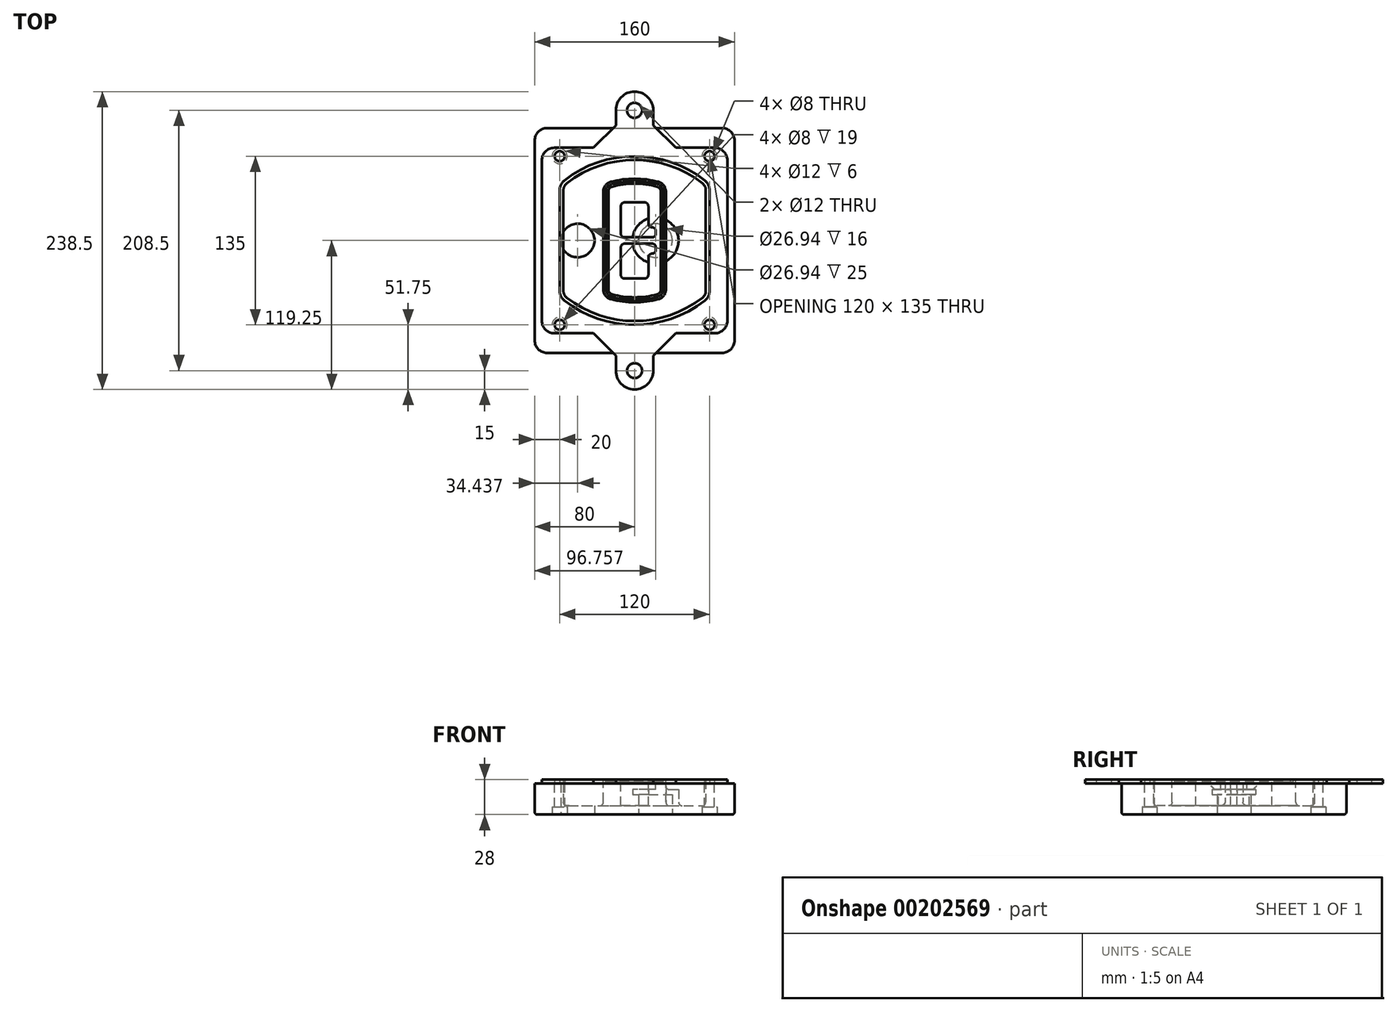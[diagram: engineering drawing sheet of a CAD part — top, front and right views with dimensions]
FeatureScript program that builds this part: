
annotation { "Feature Type Name" : "Feature", "Feature Type Description" : "" }
export const myFeature = defineFeature(function(context is Context, id is Id, definition is map)
    precondition{}
    {
        {
            var Q0;
            Q0=qCreatedBy(makeId("Top.planeOp"),FACE);
            var sketch = newSketch(context, id + "F0", { "sketchPlane" : qUnion([Q0])});
            skPoint(sketch, "E0.rect.middle", {"position": v(0, 0) * mm});
            skLineSegment(sketch, "E1.bottom", {"start": v(-70, -90) * mm, "end": v(70, -90) * mm});
            skLineSegment(sketch, "E1.top", {"start": v(-70, 90) * mm, "end": v(70, 90) * mm});
            skLineSegment(sketch, "E1.left", {"start": v(-80, -80) * mm, "end": v(-80, 80) * mm});
            skLineSegment(sketch, "E1.right", {"start": v(80, -80) * mm, "end": v(80, 80) * mm});
            skLineSegment(sketch, "E2", {"start": v(-80, 90) * mm, "end": v(80, -90) * mm, "construction": true});
            skLineSegment(sketch, "E3", {"start": v(80, 90) * mm, "end": v(-80, -90) * mm, "construction": true});
            skCircle(sketch, "E4", {"center": v(-60, 67.5) * mm, "radius": 4 * mm});
            skCircle(sketch, "E5", {"center": v(60, 67.5) * mm, "radius": 4 * mm});
            skCircle(sketch, "E6", {"center": v(60, -67.5) * mm, "radius": 4 * mm});
            skCircle(sketch, "E7", {"center": v(-60, -67.5) * mm, "radius": 4 * mm});
            skLineSegment(sketch, "E8", {"start": v(-60, 67.5) * mm, "end": v(60, 67.5) * mm, "construction": true});
            skLineSegment(sketch, "E9", {"start": v(60, 67.5) * mm, "end": v(60, -67.5) * mm, "construction": true});
            skLineSegment(sketch, "E10", {"start": v(60, -67.5) * mm, "end": v(-60, -67.5) * mm, "construction": true});
            skLineSegment(sketch, "E11", {"start": v(-60, -67.5) * mm, "end": v(-60, 67.5) * mm, "construction": true});
            skLineSegment(sketch, "E12", {"start": v(-60, 40.3) * mm, "end": v(-60, -40.3) * mm});
            skLineSegment(sketch, "E13", {"start": v(60, 40.3) * mm, "end": v(60, -40.3) * mm});
            skArc(sketch, "E14", {"start": v(56.15, 48.18) * mm, "mid": v(0, 67.5) * mm, "end": v(-56.15, 48.18) * mm});
            skArc(sketch, "E15", {"start": v(-56.15, -48.18) * mm, "mid": v(0, -67.5) * mm, "end": v(56.15, -48.18) * mm});
            skLineSegment(sketch, "E16", {"start": v(-60, 0) * mm, "end": v(60, 0) * mm, "construction": true});
            skPoint(sketch, "E17.visualSharp", {"position": v(-60, -45) * mm});
            skArc(sketch, "E17.filletArc", {"start": v(-60, -40.3) * mm, "mid": v(-58.99, -44.68) * mm, "end": v(-56.15, -48.18) * mm});
            skPoint(sketch, "E18.visualSharp", {"position": v(-60, 45) * mm});
            skArc(sketch, "E18.filletArc", {"start": v(-56.15, 48.18) * mm, "mid": v(-58.99, 44.68) * mm, "end": v(-60, 40.3) * mm});
            skPoint(sketch, "E19.visualSharp", {"position": v(60, 45) * mm});
            skArc(sketch, "E19.filletArc", {"start": v(60, 40.3) * mm, "mid": v(58.99, 44.68) * mm, "end": v(56.15, 48.18) * mm});
            skPoint(sketch, "E20.visualSharp", {"position": v(60, -45) * mm});
            skArc(sketch, "E20.filletArc", {"start": v(56.15, -48.18) * mm, "mid": v(58.99, -44.68) * mm, "end": v(60, -40.3) * mm});
            skPoint(sketch, "E21.visualSharp", {"position": v(-80, 90) * mm});
            skArc(sketch, "E21.filletArc", {"start": v(-70, 90) * mm, "mid": v(-77.07, 87.07) * mm, "end": v(-80, 80) * mm});
            skPoint(sketch, "E22.visualSharp", {"position": v(80, 90) * mm});
            skArc(sketch, "E22.filletArc", {"start": v(80, 80) * mm, "mid": v(77.07, 87.07) * mm, "end": v(70, 90) * mm});
            skPoint(sketch, "E23.visualSharp", {"position": v(80, -90) * mm});
            skArc(sketch, "E23.filletArc", {"start": v(70, -90) * mm, "mid": v(77.07, -87.07) * mm, "end": v(80, -80) * mm});
            skPoint(sketch, "E24.visualSharp", {"position": v(-80, -90) * mm});
            skArc(sketch, "E24.filletArc", {"start": v(-80, -80) * mm, "mid": v(-77.07, -87.07) * mm, "end": v(-70, -90) * mm});
            skArc(sketch, "E25.0", {"start": v(57, 40.3) * mm, "mid": v(56.3, 43.36) * mm, "end": v(54.3, 45.81) * mm});
            skLineSegment(sketch, "E25.1", {"start": v(57, 40.3) * mm, "end": v(57, -40.3) * mm});
            skArc(sketch, "E25.2", {"start": v(54.3, -45.81) * mm, "mid": v(56.3, -43.36) * mm, "end": v(57, -40.3) * mm});
            skArc(sketch, "E25.3", {"start": v(-54.3, -45.81) * mm, "mid": v(0, -64.5) * mm, "end": v(54.3, -45.81) * mm});
            skArc(sketch, "E25.4", {"start": v(-57, -40.3) * mm, "mid": v(-56.3, -43.36) * mm, "end": v(-54.3, -45.81) * mm});
            skArc(sketch, "E25.5", {"start": v(54.3, 45.81) * mm, "mid": v(0, 64.5) * mm, "end": v(-54.3, 45.81) * mm});
            skLineSegment(sketch, "E25.6", {"start": v(-57, 40.3) * mm, "end": v(-57, -40.3) * mm});
            skArc(sketch, "E25.7", {"start": v(-54.3, 45.81) * mm, "mid": v(-56.3, 43.36) * mm, "end": v(-57, 40.3) * mm});
            skArc(sketch, "E26.0", {"start": v(-58.62, 51.33) * mm, "mid": v(-62.58, 46.43) * mm, "end": v(-64, 40.3) * mm});
            skArc(sketch, "E26.1", {"start": v(58.62, 51.33) * mm, "mid": v(0, 71.5) * mm, "end": v(-58.62, 51.33) * mm});
            skArc(sketch, "E26.2", {"start": v(64, 40.3) * mm, "mid": v(62.58, 46.43) * mm, "end": v(58.62, 51.33) * mm});
            skLineSegment(sketch, "E26.3", {"start": v(64, 40.3) * mm, "end": v(64, -40.3) * mm});
            skArc(sketch, "E26.4", {"start": v(58.62, -51.33) * mm, "mid": v(62.58, -46.43) * mm, "end": v(64, -40.3) * mm});
            skLineSegment(sketch, "E26.5", {"start": v(-64, 40.3) * mm, "end": v(-64, -40.3) * mm});
            skArc(sketch, "E26.6", {"start": v(-58.62, -51.33) * mm, "mid": v(0, -71.5) * mm, "end": v(58.62, -51.33) * mm});
            skArc(sketch, "E26.7", {"start": v(-64, -40.3) * mm, "mid": v(-62.58, -46.43) * mm, "end": v(-58.62, -51.33) * mm});
            skSolve(sketch);
        }
        {
            var Q0;
            Q0=makeQuery(id+"F0.imprint","IMPRINT",FACE,{"disambiguationData":[TD([[makeQuery(id+"F0.imprint","IMPRINT",EDGE,{"derivedFrom":sQuery(id+"F0.wireOp",EDGE,"E1.bottom")}),1.0]])]});
            var Q1;
            Q1=makeQuery(id+"F0.imprint","IMPRINT",FACE,{"disambiguationData":[TD([[makeQuery(id+"F0.imprint","IMPRINT",EDGE,{"derivedFrom":sQuery(id+"F0.wireOp",EDGE,"E12")}),1.0]])]});
            var Q2;
            Q2=makeQuery(id+"F0.imprint","IMPRINT",FACE,{"disambiguationData":[TD([[makeQuery(id+"F0.imprint","IMPRINT",EDGE,{"derivedFrom":sQuery(id+"F0.wireOp",EDGE,"E25.0")}),1.0]])]});
            var Q3;
            Q3=makeQuery(id+"F0.imprint","IMPRINT",FACE,{"disambiguationData":[TD([[makeQuery(id+"F0.imprint","IMPRINT",EDGE,{"derivedFrom":sQuery(id+"F0.wireOp",EDGE,"E12")}),-1.0]])]});
            extrude(context, id + "F1", {"entities" : qUnion([Q0, Q1, Q2, Q3]), "oppositeDirection" : true, "depth" : 25 * mm});
        }
        {
            var Q0;
            Q0=makeQuery(id+"F0.imprint","IMPRINT",FACE,{"disambiguationData":[TD([[makeQuery(id+"F0.imprint","IMPRINT",EDGE,{"derivedFrom":sQuery(id+"F0.wireOp",EDGE,"E12")}),1.0]])]});
            extrude(context, id + "F2", {"entities" : qUnion([Q0]), "operationType" : NewBodyOperationType.ADD, "depth" : 3 * mm});
        }
        {
            var Q0;
            Q0=makeQuery(id+"F0.imprint","IMPRINT",FACE,{"disambiguationData":[TD([[makeQuery(id+"F0.imprint","IMPRINT",EDGE,{"derivedFrom":sQuery(id+"F0.wireOp",EDGE,"E25.0")}),1.0]])]});
            extrude(context, id + "F3", {"entities" : qUnion([Q0]), "operationType" : NewBodyOperationType.REMOVE, "oppositeDirection" : true, "depth" : 18 * mm});
        }
        {
            var Q0;
            Q0=makeQuery(id+"F2.opExtrude","CAP_FACE",FACE,{"disambiguationData":[OSD([sQuery(id+"F0.wireOp",EDGE,"E12"),sQuery(id+"F0.wireOp",EDGE,"E13"),sQuery(id+"F0.wireOp",EDGE,"E14"),sQuery(id+"F0.wireOp",EDGE,"E15"),sQuery(id+"F0.wireOp",EDGE,"E17.filletArc"),sQuery(id+"F0.wireOp",EDGE,"E18.filletArc"),sQuery(id+"F0.wireOp",EDGE,"E19.filletArc"),sQuery(id+"F0.wireOp",EDGE,"E20.filletArc"),sQuery(id+"F0.wireOp",EDGE,"E25.0"),sQuery(id+"F0.wireOp",EDGE,"E25.1"),sQuery(id+"F0.wireOp",EDGE,"E25.2"),sQuery(id+"F0.wireOp",EDGE,"E25.3"),sQuery(id+"F0.wireOp",EDGE,"E25.4"),sQuery(id+"F0.wireOp",EDGE,"E25.5"),sQuery(id+"F0.wireOp",EDGE,"E25.6"),sQuery(id+"F0.wireOp",EDGE,"E25.7")])],"isStart":false});
            var sketch = newSketch(context, id + "F4", { "sketchPlane" : qUnion([Q0])});
            skArc(sketch, "E27.0", {"start": v(-19.08, -46.97) * mm, "mid": v(0, -49.5) * mm, "end": v(19.08, -46.97) * mm});
            skArc(sketch, "E28.0", {"start": v(19.08, 46.97) * mm, "mid": v(0, 49.5) * mm, "end": v(-19.08, 46.97) * mm});
            skLineSegment(sketch, "E29", {"start": v(-25, 39.25) * mm, "end": v(-25, -39.25) * mm});
            skLineSegment(sketch, "E30", {"start": v(25, 39.25) * mm, "end": v(25, -39.25) * mm});
            skLineSegment(sketch, "E31", {"start": v(-25, 45.1) * mm, "end": v(25, 45.1) * mm, "construction": true});
            skLineSegment(sketch, "E32", {"start": v(-25, -45.1) * mm, "end": v(25, -45.1) * mm, "construction": true});
            skPoint(sketch, "E33.visualSharp", {"position": v(-25, 45.1) * mm});
            skArc(sketch, "E33.filletArc", {"start": v(-19.08, 46.97) * mm, "mid": v(-23.35, 44.11) * mm, "end": v(-25, 39.25) * mm});
            skPoint(sketch, "E34.visualSharp", {"position": v(25, 45.1) * mm});
            skArc(sketch, "E34.filletArc", {"start": v(25, 39.25) * mm, "mid": v(23.35, 44.11) * mm, "end": v(19.08, 46.97) * mm});
            skPoint(sketch, "E35.visualSharp", {"position": v(25, -45.1) * mm});
            skArc(sketch, "E35.filletArc", {"start": v(19.08, -46.97) * mm, "mid": v(23.35, -44.11) * mm, "end": v(25, -39.25) * mm});
            skPoint(sketch, "E36.visualSharp", {"position": v(-25, -45.1) * mm});
            skArc(sketch, "E36.filletArc", {"start": v(-25, -39.25) * mm, "mid": v(-23.35, -44.11) * mm, "end": v(-19.08, -46.97) * mm});
            skArc(sketch, "E37.0", {"start": v(54.3, 45.81) * mm, "mid": v(0, 64.5) * mm, "end": v(-54.3, 45.81) * mm});
            skArc(sketch, "E37.1", {"start": v(-54.3, 45.81) * mm, "mid": v(-56.3, 43.36) * mm, "end": v(-57, 40.3) * mm});
            skLineSegment(sketch, "E37.2", {"start": v(-57, 40.3) * mm, "end": v(-57, -40.3) * mm});
            skArc(sketch, "E37.3", {"start": v(-57, -40.3) * mm, "mid": v(-56.3, -43.36) * mm, "end": v(-54.3, -45.81) * mm});
            skArc(sketch, "E37.4", {"start": v(-54.3, -45.81) * mm, "mid": v(0, -64.5) * mm, "end": v(54.3, -45.81) * mm});
            skArc(sketch, "E37.5", {"start": v(54.3, -45.81) * mm, "mid": v(56.3, -43.36) * mm, "end": v(57, -40.3) * mm});
            skLineSegment(sketch, "E37.6", {"start": v(57, 40.3) * mm, "end": v(57, -40.3) * mm});
            skArc(sketch, "E37.7", {"start": v(57, 40.3) * mm, "mid": v(56.3, 43.36) * mm, "end": v(54.3, 45.81) * mm});
            skLineSegment(sketch, "E38.0", {"start": v(23, 39.25) * mm, "end": v(23, -39.25) * mm});
            skArc(sketch, "E38.1", {"start": v(18.56, -45.04) * mm, "mid": v(21.76, -42.9) * mm, "end": v(23, -39.25) * mm});
            skArc(sketch, "E38.2", {"start": v(-18.56, -45.04) * mm, "mid": v(0, -47.5) * mm, "end": v(18.56, -45.04) * mm});
            skArc(sketch, "E38.3", {"start": v(-23, -39.25) * mm, "mid": v(-21.76, -42.9) * mm, "end": v(-18.56, -45.04) * mm});
            skLineSegment(sketch, "E38.4", {"start": v(-23, 39.25) * mm, "end": v(-23, -39.25) * mm});
            skArc(sketch, "E38.5", {"start": v(23, 39.25) * mm, "mid": v(21.76, 42.9) * mm, "end": v(18.56, 45.04) * mm});
            skArc(sketch, "E38.6", {"start": v(-18.56, 45.04) * mm, "mid": v(-21.76, 42.9) * mm, "end": v(-23, 39.25) * mm});
            skArc(sketch, "E38.7", {"start": v(18.56, 45.04) * mm, "mid": v(0, 47.5) * mm, "end": v(-18.56, 45.04) * mm});
            skArc(sketch, "E39.0", {"start": v(21, 39.25) * mm, "mid": v(20.18, 41.68) * mm, "end": v(18.04, 43.1) * mm});
            skLineSegment(sketch, "E39.1", {"start": v(21, 39.25) * mm, "end": v(21, -39.25) * mm});
            skArc(sketch, "E39.2", {"start": v(18.04, -43.1) * mm, "mid": v(20.18, -41.68) * mm, "end": v(21, -39.25) * mm});
            skArc(sketch, "E39.3", {"start": v(-18.04, -43.1) * mm, "mid": v(0, -45.5) * mm, "end": v(18.04, -43.1) * mm});
            skArc(sketch, "E39.4", {"start": v(-21, -39.25) * mm, "mid": v(-20.18, -41.68) * mm, "end": v(-18.04, -43.1) * mm});
            skArc(sketch, "E39.5", {"start": v(18.04, 43.1) * mm, "mid": v(0, 45.5) * mm, "end": v(-18.04, 43.1) * mm});
            skLineSegment(sketch, "E39.6", {"start": v(-21, 39.25) * mm, "end": v(-21, -39.25) * mm});
            skArc(sketch, "E39.7", {"start": v(-18.04, 43.1) * mm, "mid": v(-20.18, 41.68) * mm, "end": v(-21, 39.25) * mm});
            skLineSegment(sketch, "E40", {"start": v(-25, 0) * mm, "end": v(25, 0) * mm, "construction": true});
            skLineSegment(sketch, "E41", {"start": v(-11, 5.5) * mm, "end": v(-11, 27.5) * mm});
            skLineSegment(sketch, "E42", {"start": v(-8, 30.5) * mm, "end": v(8, 30.5) * mm});
            skLineSegment(sketch, "E43", {"start": v(11, 27.5) * mm, "end": v(11, 13.5) * mm});
            skLineSegment(sketch, "E44", {"start": v(14, 10.5) * mm, "end": v(14, 10.5) * mm});
            skLineSegment(sketch, "E45", {"start": v(17, 7.5) * mm, "end": v(17, 5.5) * mm});
            skLineSegment(sketch, "E46", {"start": v(14, 2.5) * mm, "end": v(-8, 2.5) * mm});
            skPoint(sketch, "E47.visualSharp", {"position": v(-11, 30.5) * mm});
            skArc(sketch, "E47.filletArc", {"start": v(-8, 30.5) * mm, "mid": v(-10.12, 29.62) * mm, "end": v(-11, 27.5) * mm});
            skPoint(sketch, "E48.visualSharp", {"position": v(11, 30.5) * mm});
            skArc(sketch, "E48.filletArc", {"start": v(11, 27.5) * mm, "mid": v(10.12, 29.62) * mm, "end": v(8, 30.5) * mm});
            skPoint(sketch, "E49.visualSharp", {"position": v(11, 10.5) * mm});
            skArc(sketch, "E49.filletArc", {"start": v(11, 13.5) * mm, "mid": v(11.88, 11.38) * mm, "end": v(14, 10.5) * mm});
            skPoint(sketch, "E50.visualSharp", {"position": v(17, 10.5) * mm});
            skArc(sketch, "E50.filletArc", {"start": v(17, 7.5) * mm, "mid": v(16.12, 9.62) * mm, "end": v(14, 10.5) * mm});
            skPoint(sketch, "E51.visualSharp", {"position": v(17, 2.5) * mm});
            skArc(sketch, "E51.filletArc", {"start": v(14, 2.5) * mm, "mid": v(16.12, 3.38) * mm, "end": v(17, 5.5) * mm});
            skPoint(sketch, "E52.visualSharp", {"position": v(-11, 2.5) * mm});
            skArc(sketch, "E52.filletArc", {"start": v(-11, 5.5) * mm, "mid": v(-10.12, 3.38) * mm, "end": v(-8, 2.5) * mm});
            skLineSegment(sketch, "E53.0.MirrorCS", {"start": v(14, -2.5) * mm, "end": v(-8, -2.5) * mm});
            skArc(sketch, "E54.0.MirrorCS", {"start": v(-11, -5.5) * mm, "mid": v(-10.12, -3.38) * mm, "end": v(-8, -2.5) * mm});
            skLineSegment(sketch, "E55.0.MirrorCS", {"start": v(-11, -5.5) * mm, "end": v(-11, -27.5) * mm});
            skArc(sketch, "E56.0.MirrorCS", {"start": v(-8, -30.5) * mm, "mid": v(-10.12, -29.62) * mm, "end": v(-11, -27.5) * mm});
            skLineSegment(sketch, "E57.0.MirrorCS", {"start": v(-8, -30.5) * mm, "end": v(8, -30.5) * mm});
            skArc(sketch, "E58.0.MirrorCS", {"start": v(11, -27.5) * mm, "mid": v(10.12, -29.62) * mm, "end": v(8, -30.5) * mm});
            skLineSegment(sketch, "E59.0.MirrorCS", {"start": v(11, -27.5) * mm, "end": v(11, -13.5) * mm});
            skArc(sketch, "E60.0.MirrorCS", {"start": v(11, -13.5) * mm, "mid": v(11.88, -11.38) * mm, "end": v(14, -10.5) * mm});
            skArc(sketch, "E61.0.MirrorCS", {"start": v(17, -7.5) * mm, "mid": v(16.12, -9.62) * mm, "end": v(14, -10.5) * mm});
            skLineSegment(sketch, "E62.0.MirrorCS", {"start": v(17, -7.5) * mm, "end": v(17, -5.5) * mm});
            skArc(sketch, "E63.0.MirrorCS", {"start": v(14, -2.5) * mm, "mid": v(16.12, -3.38) * mm, "end": v(17, -5.5) * mm});
            skSolve(sketch);
        }
        {
            var Q0;
            Q0=makeQuery(id+"F4.imprint","IMPRINT",FACE,{"disambiguationData":[TD([[makeQuery(id+"F4.imprint","IMPRINT",EDGE,{"derivedFrom":sQuery(id+"F4.wireOp",EDGE,"E27.0")}),1.0]])]});
            var Q1;
            Q1=makeQuery(id+"F4.imprint","IMPRINT",FACE,{"disambiguationData":[TD([[makeQuery(id+"F4.imprint","IMPRINT",EDGE,{"derivedFrom":sQuery(id+"F4.wireOp",EDGE,"E38.0")}),-1.0]])]});
            var Q2;
            Q2=makeQuery(id+"F4.imprint","IMPRINT",FACE,{"disambiguationData":[TD([[makeQuery(id+"F4.imprint","IMPRINT",EDGE,{"derivedFrom":sQuery(id+"F4.wireOp",EDGE,"E39.0")}),1.0]])]});
            extrude(context, id + "F5", {"entities" : qUnion([Q0, Q1, Q2]), "operationType" : NewBodyOperationType.ADD, "endBound" : BoundingType.UP_TO_NEXT, "oppositeDirection" : true, "depth" : 25 * mm});
        }
        {
            var Q0;
            Q0=makeQuery(id+"F4.imprint","IMPRINT",FACE,{"disambiguationData":[TD([[makeQuery(id+"F4.imprint","IMPRINT",EDGE,{"derivedFrom":sQuery(id+"F4.wireOp",EDGE,"E38.0")}),-1.0]])]});
            extrude(context, id + "F6", {"entities" : qUnion([Q0]), "operationType" : NewBodyOperationType.REMOVE, "oppositeDirection" : true, "depth" : 2 * mm});
        }
        {
            var Q0;
            Q0=makeQuery(id+"F1.opExtrude","CAP_FACE",FACE,{"disambiguationData":[OSD([sQuery(id+"F0.wireOp",EDGE,"E1.bottom"),sQuery(id+"F0.wireOp",EDGE,"E1.top"),sQuery(id+"F0.wireOp",EDGE,"E1.left"),sQuery(id+"F0.wireOp",EDGE,"E1.right"),sQuery(id+"F0.wireOp",EDGE,"E4"),sQuery(id+"F0.wireOp",EDGE,"E5"),sQuery(id+"F0.wireOp",EDGE,"E6"),sQuery(id+"F0.wireOp",EDGE,"E7"),sQuery(id+"F0.wireOp",EDGE,"E21.filletArc"),sQuery(id+"F0.wireOp",EDGE,"E22.filletArc"),sQuery(id+"F0.wireOp",EDGE,"E23.filletArc"),sQuery(id+"F0.wireOp",EDGE,"E24.filletArc")])],"isStart":false});
            var sketch = newSketch(context, id + "F7", { "sketchPlane" : qUnion([Q0])});
            skCircle(sketch, "E64", {"center": v(16.76, 0) * mm, "radius": 13.47 * mm});
            skCircle(sketch, "E65", {"center": v(-45.56, 0) * mm, "radius": 13.47 * mm});
            skLineSegment(sketch, "E66", {"start": v(80, 0) * mm, "end": v(-80, 0) * mm});
            skCircle(sketch, "E67", {"center": v(16.76, 0) * mm, "radius": 18.47 * mm});
            skCircle(sketch, "E68", {"center": v(60, -67.5) * mm, "radius": 6 * mm});
            skCircle(sketch, "E69", {"center": v(-60, -67.5) * mm, "radius": 6 * mm});
            skCircle(sketch, "E70", {"center": v(-60, 67.5) * mm, "radius": 6 * mm});
            skCircle(sketch, "E71", {"center": v(60, 67.5) * mm, "radius": 6 * mm});
            skSolve(sketch);
        }
        {
            var Q0;
            {var subQ1=sQuery(id+"F7.wireOp",EDGE,"E66");var subQ4=sQuery(id+"F7.wireOp",EDGE,"E64");var subQ6=makeQuery(id+"F7.imprint","INTERSECT",VERTEX,{"disambiguationData":[OD(0.0)],"derivedFrom":[subQ4,subQ1]});Q0=makeQuery(id+"F7.imprint","IMPRINT",FACE,{"disambiguationData":[TD([[makeQuery(id+"F7.imprint","IMPRINT",EDGE,{"disambiguationData":[TD([[subQ6,-1.0]])],"derivedFrom":subQ4}),-1.0]])]});}
            var Q1;
            {var subQ0=sQuery(id+"F7.wireOp",EDGE,"E66");var subQ1=sQuery(id+"F7.wireOp",EDGE,"E64");var subQ3=makeQuery(id+"F7.imprint","INTERSECT",VERTEX,{"disambiguationData":[OD(0.0)],"derivedFrom":[subQ1,subQ0]});Q1=makeQuery(id+"F7.imprint","IMPRINT",FACE,{"disambiguationData":[TD([[makeQuery(id+"F7.imprint","IMPRINT",EDGE,{"disambiguationData":[TD([[subQ3,-1.0]])],"derivedFrom":subQ1}),1.0]])]});}
            var Q2;
            {var subQ0=sQuery(id+"F7.wireOp",EDGE,"E66");var subQ1=sQuery(id+"F7.wireOp",EDGE,"E64");var subQ3=makeQuery(id+"F7.imprint","INTERSECT",VERTEX,{"disambiguationData":[OD(0.0)],"derivedFrom":[subQ1,subQ0]});Q2=makeQuery(id+"F7.imprint","IMPRINT",FACE,{"disambiguationData":[TD([[makeQuery(id+"F7.imprint","IMPRINT",EDGE,{"disambiguationData":[TD([[subQ3,1.0]])],"derivedFrom":subQ1}),1.0]])]});}
            var Q3;
            {var subQ1=sQuery(id+"F7.wireOp",EDGE,"E66");var subQ4=sQuery(id+"F7.wireOp",EDGE,"E64");var subQ6=makeQuery(id+"F7.imprint","INTERSECT",VERTEX,{"disambiguationData":[OD(0.0)],"derivedFrom":[subQ4,subQ1]});Q3=makeQuery(id+"F7.imprint","IMPRINT",FACE,{"disambiguationData":[TD([[makeQuery(id+"F7.imprint","IMPRINT",EDGE,{"disambiguationData":[TD([[subQ6,1.0]])],"derivedFrom":subQ4}),-1.0]])]});}
            extrude(context, id + "F8", {"entities" : qUnion([Q0, Q1, Q2, Q3]), "operationType" : NewBodyOperationType.ADD, "oppositeDirection" : true, "depth" : 20 * mm});
        }
        {
            var Q0;
            {var subQ0=sQuery(id+"F7.wireOp",EDGE,"E66");var subQ1=sQuery(id+"F7.wireOp",EDGE,"E64");var subQ3=makeQuery(id+"F7.imprint","INTERSECT",VERTEX,{"disambiguationData":[OD(0.0)],"derivedFrom":[subQ1,subQ0]});Q0=makeQuery(id+"F7.imprint","IMPRINT",FACE,{"disambiguationData":[TD([[makeQuery(id+"F7.imprint","IMPRINT",EDGE,{"disambiguationData":[TD([[subQ3,-1.0]])],"derivedFrom":subQ1}),1.0]])]});}
            var Q1;
            {var subQ0=sQuery(id+"F7.wireOp",EDGE,"E66");var subQ1=sQuery(id+"F7.wireOp",EDGE,"E64");var subQ3=makeQuery(id+"F7.imprint","INTERSECT",VERTEX,{"disambiguationData":[OD(0.0)],"derivedFrom":[subQ1,subQ0]});Q1=makeQuery(id+"F7.imprint","IMPRINT",FACE,{"disambiguationData":[TD([[makeQuery(id+"F7.imprint","IMPRINT",EDGE,{"disambiguationData":[TD([[subQ3,1.0]])],"derivedFrom":subQ1}),1.0]])]});}
            extrude(context, id + "F9", {"entities" : qUnion([Q0, Q1]), "operationType" : NewBodyOperationType.REMOVE, "oppositeDirection" : true, "depth" : 16 * mm});
        }
        {
            var Q0;
            {var subQ0=sQuery(id+"F7.wireOp",EDGE,"E66");var subQ1=sQuery(id+"F7.wireOp",EDGE,"E65");var subQ3=makeQuery(id+"F7.imprint","INTERSECT",VERTEX,{"disambiguationData":[OD(0.0)],"derivedFrom":[subQ1,subQ0]});Q0=makeQuery(id+"F7.imprint","IMPRINT",FACE,{"disambiguationData":[TD([[makeQuery(id+"F7.imprint","IMPRINT",EDGE,{"disambiguationData":[TD([[subQ3,-1.0]])],"derivedFrom":subQ1}),1.0]])]});}
            var Q1;
            {var subQ0=sQuery(id+"F7.wireOp",EDGE,"E66");var subQ1=sQuery(id+"F7.wireOp",EDGE,"E65");var subQ3=makeQuery(id+"F7.imprint","INTERSECT",VERTEX,{"disambiguationData":[OD(0.0)],"derivedFrom":[subQ1,subQ0]});Q1=makeQuery(id+"F7.imprint","IMPRINT",FACE,{"disambiguationData":[TD([[makeQuery(id+"F7.imprint","IMPRINT",EDGE,{"disambiguationData":[TD([[subQ3,1.0]])],"derivedFrom":subQ1}),1.0]])]});}
            extrude(context, id + "F10", {"entities" : qUnion([Q0, Q1]), "operationType" : NewBodyOperationType.REMOVE, "oppositeDirection" : true, "depth" : 25 * mm});
        }
        {
            var Q0;
            Q0=makeQuery(id+"F7.imprint","IMPRINT",FACE,{"disambiguationData":[TD([[makeQuery(id+"F7.imprint","IMPRINT",EDGE,{"derivedFrom":sQuery(id+"F7.wireOp",EDGE,"E68")}),1.0]])]});
            var Q1;
            Q1=makeQuery(id+"F7.imprint","IMPRINT",FACE,{"disambiguationData":[TD([[makeQuery(id+"F7.imprint","IMPRINT",EDGE,{"derivedFrom":makeQuery(id+"F1.opExtrude","CAP_EDGE",EDGE,{"disambiguationData":[OSD([sQuery(id+"F0.wireOp",EDGE,"E5")])],"isStart":false})}),-1.0]])]});
            var Q2;
            Q2=makeQuery(id+"F7.imprint","IMPRINT",FACE,{"disambiguationData":[TD([[makeQuery(id+"F7.imprint","IMPRINT",EDGE,{"derivedFrom":sQuery(id+"F7.wireOp",EDGE,"E69")}),1.0]])]});
            var Q3;
            Q3=makeQuery(id+"F7.imprint","IMPRINT",FACE,{"disambiguationData":[TD([[makeQuery(id+"F7.imprint","IMPRINT",EDGE,{"derivedFrom":makeQuery(id+"F1.opExtrude","CAP_EDGE",EDGE,{"disambiguationData":[OSD([sQuery(id+"F0.wireOp",EDGE,"E4")])],"isStart":false})}),-1.0]])]});
            var Q4;
            Q4=makeQuery(id+"F7.imprint","IMPRINT",FACE,{"disambiguationData":[TD([[makeQuery(id+"F7.imprint","IMPRINT",EDGE,{"derivedFrom":sQuery(id+"F7.wireOp",EDGE,"E70")}),1.0]])]});
            var Q5;
            Q5=makeQuery(id+"F7.imprint","IMPRINT",FACE,{"disambiguationData":[TD([[makeQuery(id+"F7.imprint","IMPRINT",EDGE,{"derivedFrom":makeQuery(id+"F1.opExtrude","CAP_EDGE",EDGE,{"disambiguationData":[OSD([sQuery(id+"F0.wireOp",EDGE,"E7")])],"isStart":false})}),-1.0]])]});
            var Q6;
            Q6=makeQuery(id+"F7.imprint","IMPRINT",FACE,{"disambiguationData":[TD([[makeQuery(id+"F7.imprint","IMPRINT",EDGE,{"derivedFrom":sQuery(id+"F7.wireOp",EDGE,"E71")}),1.0]])]});
            var Q7;
            Q7=makeQuery(id+"F7.imprint","IMPRINT",FACE,{"disambiguationData":[TD([[makeQuery(id+"F7.imprint","IMPRINT",EDGE,{"derivedFrom":makeQuery(id+"F1.opExtrude","CAP_EDGE",EDGE,{"disambiguationData":[OSD([sQuery(id+"F0.wireOp",EDGE,"E6")])],"isStart":false})}),-1.0]])]});
            extrude(context, id + "F11", {"entities" : qUnion([Q0, Q1, Q2, Q3, Q4, Q5, Q6, Q7]), "operationType" : NewBodyOperationType.REMOVE, "oppositeDirection" : true, "depth" : 6 * mm});
        }
        {
            var Q0;
            Q0=makeQuery(id+"F9.boolean.opBoolean","COPY",FACE,{"derivedFrom":makeQuery(id+"F9.opExtrude","CAP_FACE",FACE,{"disambiguationData":[OSD([sQuery(id+"F7.wireOp",EDGE,"E64")])],"isStart":false})});
            var sketch = newSketch(context, id + "F12", { "sketchPlane" : qUnion([Q0])});
            skArc(sketch, "E72.0", {"start": v(11, 17.55) * mm, "mid": v(2.57, 11.82) * mm, "end": v(-1.54, 2.5) * mm});
            skArc(sketch, "E72.1", {"start": v(-1.54, -2.5) * mm, "mid": v(2.57, -11.82) * mm, "end": v(11, -17.55) * mm});
            skLineSegment(sketch, "E73", {"start": v(-1.54, -2.5) * mm, "end": v(14, -2.5) * mm});
            skLineSegment(sketch, "E74.0", {"start": v(14, 2.5) * mm, "end": v(-1.54, 2.5) * mm});
            skArc(sketch, "E74.1", {"start": v(14, 2.5) * mm, "mid": v(16.12, 3.38) * mm, "end": v(17, 5.5) * mm});
            skLineSegment(sketch, "E74.2", {"start": v(17, 7.5) * mm, "end": v(17, 5.5) * mm});
            skArc(sketch, "E74.3", {"start": v(17, 7.5) * mm, "mid": v(16.12, 9.62) * mm, "end": v(14, 10.5) * mm});
            skArc(sketch, "E74.4", {"start": v(11, 13.5) * mm, "mid": v(11.88, 11.38) * mm, "end": v(14, 10.5) * mm});
            skLineSegment(sketch, "E74.5", {"start": v(11, 17.55) * mm, "end": v(11, 13.5) * mm});
            skLineSegment(sketch, "E74.7", {"start": v(14, -2.5) * mm, "end": v(-1.54, -2.5) * mm});
            skArc(sketch, "E74.8", {"start": v(14, -2.5) * mm, "mid": v(16.12, -3.38) * mm, "end": v(17, -5.5) * mm});
            skLineSegment(sketch, "E74.9", {"start": v(17, -7.5) * mm, "end": v(17, -5.5) * mm});
            skArc(sketch, "E74.10", {"start": v(17, -7.5) * mm, "mid": v(16.12, -9.62) * mm, "end": v(14, -10.5) * mm});
            skArc(sketch, "E74.11", {"start": v(11, -13.5) * mm, "mid": v(11.88, -11.38) * mm, "end": v(14, -10.5) * mm});
            skLineSegment(sketch, "E74.12", {"start": v(11, -17.55) * mm, "end": v(11, -13.5) * mm});
            skPoint(sketch, "E75.orphan", {"position": v(11, -27.5) * mm});
            skPoint(sketch, "E76.orphan", {"position": v(-8, -2.5) * mm});
            skPoint(sketch, "E77.orphan", {"position": v(-8, 2.5) * mm});
            skPoint(sketch, "E78.orphan", {"position": v(11, 27.5) * mm});
            skSolve(sketch);
        }
        {
            var Q0;
            {var subQ7=sQuery(id+"F12.wireOp",EDGE,"E72.0");var subQ14=sQuery(id+"F12.wireOp",EDGE,"E72.1");var subQ16=sQuery(id+"F12.wireOp",EDGE,"E74.1");var subQ18=sQuery(id+"F12.wireOp",EDGE,"E74.8");Q0=qUnion([makeQuery(id+"F12.imprint","IMPRINT",FACE,{"disambiguationData":[TD([[makeQuery(id+"F12.imprint","IMPRINT",EDGE,{"derivedFrom":subQ7}),1.0]])]}),makeQuery(id+"F12.imprint","IMPRINT",FACE,{"disambiguationData":[TD([[makeQuery(id+"F12.imprint","IMPRINT",EDGE,{"derivedFrom":subQ14}),1.0]])]}),makeQuery(id+"F12.imprint","IMPRINT",FACE,{"disambiguationData":[TD([[makeQuery(id+"F12.imprint","IMPRINT",EDGE,{"derivedFrom":subQ16}),1.0]])]}),makeQuery(id+"F12.imprint","IMPRINT",FACE,{"disambiguationData":[TD([[makeQuery(id+"F12.imprint","IMPRINT",EDGE,{"derivedFrom":subQ18}),-1.0]])]})]);}
            var Q1;
            Q1=makeQuery(id+"F5.boolean.opBoolean","SPLIT",FACE,{"disambiguationData":[TD([makeQuery(id+"F5.opExtrude","SWEPT_FACE",FACE,{"disambiguationData":[OSD([sQuery(id+"F4.wireOp",EDGE,"E41")])]})])],"derivedFrom":makeQuery(id+"F3.boolean.opBoolean","COPY",FACE,{"derivedFrom":makeQuery(id+"F3.opExtrude","CAP_FACE",FACE,{"disambiguationData":[OSD([sQuery(id+"F0.wireOp",EDGE,"E25.0"),sQuery(id+"F0.wireOp",EDGE,"E25.1"),sQuery(id+"F0.wireOp",EDGE,"E25.2"),sQuery(id+"F0.wireOp",EDGE,"E25.3"),sQuery(id+"F0.wireOp",EDGE,"E25.4"),sQuery(id+"F0.wireOp",EDGE,"E25.5"),sQuery(id+"F0.wireOp",EDGE,"E25.6"),sQuery(id+"F0.wireOp",EDGE,"E25.7")])],"isStart":false})})});
            extrude(context, id + "F13", {"entities" : qUnion([Q0]), "operationType" : NewBodyOperationType.REMOVE, "endBound" : BoundingType.UP_TO_SURFACE, "endBoundEntityFace" : qUnion([Q1]), "depth" : 25 * mm});
        }
        {
            var Q0;
            Q0=makeQuery(id+"F3.boolean.opBoolean","COPY",EDGE,{"derivedFrom":makeQuery(id+"F3.opExtrude","CAP_EDGE",EDGE,{"disambiguationData":[OSD([sQuery(id+"F0.wireOp",EDGE,"E25.6")])],"isStart":false})});
            var Q1;
            Q1=makeQuery(id+"F8.boolean.opBoolean","INTERSECT",EDGE,{"derivedFrom":[makeQuery(id+"F5.opExtrude","SWEPT_FACE",FACE,{"disambiguationData":[OSD([sQuery(id+"F4.wireOp",EDGE,"E30")])]}),makeQuery(id+"F8.opExtrude","CAP_FACE",FACE,{"disambiguationData":[OSD([sQuery(id+"F7.wireOp",EDGE,"E67")])],"isStart":false})]});
            var Q2;
            Q2=makeQuery(id+"F8.boolean.opBoolean","INTERSECT",EDGE,{"disambiguationData":[OD(1.0)],"derivedFrom":[makeQuery(id+"F5.opExtrude","SWEPT_FACE",FACE,{"disambiguationData":[OSD([sQuery(id+"F4.wireOp",EDGE,"E30")])]}),makeQuery(id+"F8.opExtrude","SWEPT_FACE",FACE,{"disambiguationData":[OSD([sQuery(id+"F7.wireOp",EDGE,"E67")])]})]});
            var Q3;
            {var subQ0=sQuery(id+"F4.wireOp",EDGE,"E30");Q3=makeQuery(id+"F8.boolean.opBoolean","SPLIT",EDGE,{"disambiguationData":[TD([makeQuery(id+"F5.opExtrude","SWEPT_FACE",FACE,{"disambiguationData":[OSD([sQuery(id+"F4.wireOp",EDGE,"E35.filletArc")])]})])],"derivedFrom":makeQuery(id+"F5.opExtrude","CAP_EDGE",EDGE,{"disambiguationData":[OSD([subQ0])],"isStart":false})});}
            var Q4;
            {var subQ0=sQuery(id+"F0.wireOp",EDGE,"E25.7");var subQ1=sQuery(id+"F0.wireOp",EDGE,"E25.1");var subQ2=sQuery(id+"F0.wireOp",EDGE,"E25.6");var subQ3=sQuery(id+"F0.wireOp",EDGE,"E25.5");var subQ4=sQuery(id+"F0.wireOp",EDGE,"E25.4");var subQ5=sQuery(id+"F0.wireOp",EDGE,"E25.0");var subQ6=sQuery(id+"F0.wireOp",EDGE,"E25.2");var subQ7=sQuery(id+"F0.wireOp",EDGE,"E25.3");Q4=makeQuery(id+"F8.boolean.opBoolean","INTERSECT",EDGE,{"derivedFrom":[makeQuery(id+"F5.boolean.opBoolean","SPLIT",FACE,{"disambiguationData":[TD([makeQuery(id+"F2.opExtrude","SWEPT_FACE",FACE,{"disambiguationData":[OSD([subQ5])]})])],"derivedFrom":makeQuery(id+"F3.boolean.opBoolean","COPY",FACE,{"derivedFrom":makeQuery(id+"F3.opExtrude","CAP_FACE",FACE,{"disambiguationData":[OSD([subQ5,subQ1,subQ6,subQ7,subQ4,subQ3,subQ2,subQ0])],"isStart":false})})}),makeQuery(id+"F8.opExtrude","SWEPT_FACE",FACE,{"disambiguationData":[OSD([sQuery(id+"F7.wireOp",EDGE,"E67")])]})]});}
            var Q5;
            Q5=makeQuery(id+"F8.boolean.opBoolean","INTERSECT",EDGE,{"disambiguationData":[OD(0.0)],"derivedFrom":[makeQuery(id+"F5.opExtrude","SWEPT_FACE",FACE,{"disambiguationData":[OSD([sQuery(id+"F4.wireOp",EDGE,"E30")])]}),makeQuery(id+"F8.opExtrude","SWEPT_FACE",FACE,{"disambiguationData":[OSD([sQuery(id+"F7.wireOp",EDGE,"E67")])]})]});
            fillet(context, id + "F14", {"entities" : qUnion([Q0, Q1, Q2, Q3, Q4, Q5]), "radius" : 3 * mm, "tangentPropagation" : true, "allowEdgeOverflow" : false});
        }
        {
            var Q0;
            Q0=makeQuery(id+"F1.opExtrude","CAP_EDGE",EDGE,{"disambiguationData":[OSD([sQuery(id+"F0.wireOp",EDGE,"E1.bottom")])],"isStart":false});
            fillet(context, id + "F15", {"entities" : qUnion([Q0]), "radius" : 2 * mm, "tangentPropagation" : true, "allowEdgeOverflow" : false});
        }
        {
            var Q0;
            {var subQ0=sQuery(id+"F0.wireOp",EDGE,"E22.filletArc");var subQ1=sQuery(id+"F0.wireOp",EDGE,"E7");var subQ2=sQuery(id+"F0.wireOp",EDGE,"E6");var subQ3=sQuery(id+"F0.wireOp",EDGE,"E5");var subQ4=sQuery(id+"F0.wireOp",EDGE,"E4");var subQ5=sQuery(id+"F0.wireOp",EDGE,"E1.bottom");var subQ6=sQuery(id+"F0.wireOp",EDGE,"E21.filletArc");var subQ7=sQuery(id+"F0.wireOp",EDGE,"E1.top");var subQ8=sQuery(id+"F0.wireOp",EDGE,"E1.left");var subQ9=sQuery(id+"F0.wireOp",EDGE,"E1.right");var subQ10=sQuery(id+"F0.wireOp",EDGE,"E23.filletArc");var subQ11=sQuery(id+"F0.wireOp",EDGE,"E24.filletArc");Q0=makeQuery(id+"F2.boolean.opBoolean","SPLIT",FACE,{"disambiguationData":[TD([makeQuery(id+"F1.opExtrude","SWEPT_FACE",FACE,{"disambiguationData":[OSD([subQ5])]})])],"derivedFrom":makeQuery(id+"F1.opExtrude","CAP_FACE",FACE,{"disambiguationData":[OSD([subQ5,subQ7,subQ8,subQ9,subQ4,subQ3,subQ2,subQ1,subQ6,subQ0,subQ10,subQ11])],"isStart":true})});}
            var sketch = newSketch(context, id + "F16", { "sketchPlane" : qUnion([Q0])});
            skLineSegment(sketch, "E79", {"start": v(33, 74.25) * mm, "end": v(15, 92.25) * mm});
            skLineSegment(sketch, "E80", {"start": v(15, 92.25) * mm, "end": v(15, 104.25) * mm});
            skCircle(sketch, "E81", {"center": v(0, 104.25) * mm, "radius": 6 * mm});
            skLineSegment(sketch, "E82", {"start": v(-33, 74.25) * mm, "end": v(-15, 92.25) * mm});
            skLineSegment(sketch, "E83", {"start": v(-15, 92.25) * mm, "end": v(-15, 104.25) * mm});
            skArc(sketch, "E84", {"start": v(15, 104.25) * mm, "mid": v(0, 119.25) * mm, "end": v(-15, 104.25) * mm});
            skLineSegment(sketch, "E85", {"start": v(0, 104.25) * mm, "end": v(0, 74.25) * mm, "construction": true});
            skLineSegment(sketch, "E86", {"start": v(-74.25, 0) * mm, "end": v(74.25, 0) * mm, "construction": true});
            skLineSegment(sketch, "E87.MirrorCS", {"start": v(-33, -74.25) * mm, "end": v(-15, -92.25) * mm});
            skLineSegment(sketch, "E88.MirrorCS", {"start": v(-15, -92.25) * mm, "end": v(-15, -104.25) * mm});
            skArc(sketch, "E89.MirrorCS", {"start": v(15, -104.25) * mm, "mid": v(0, -119.25) * mm, "end": v(-15, -104.25) * mm});
            skLineSegment(sketch, "E90.MirrorCS", {"start": v(15, -92.25) * mm, "end": v(15, -104.25) * mm});
            skLineSegment(sketch, "E91.MirrorCS", {"start": v(33, -74.25) * mm, "end": v(15, -92.25) * mm});
            skLineSegment(sketch, "E92.MirrorCS", {"start": v(0, -104.25) * mm, "end": v(0, -74.25) * mm, "construction": true});
            skCircle(sketch, "E93.MirrorC", {"center": v(0, -104.25) * mm, "radius": 6 * mm});
            skArc(sketch, "E94.0", {"start": v(-64.25, 74.25) * mm, "mid": v(-71.32, 71.32) * mm, "end": v(-74.25, 64.25) * mm});
            skLineSegment(sketch, "E94.1", {"start": v(-74.25, -64.25) * mm, "end": v(-74.25, 64.25) * mm});
            skLineSegment(sketch, "E94.2", {"start": v(-64.25, 74.25) * mm, "end": v(64.25, 74.25) * mm});
            skArc(sketch, "E94.3", {"start": v(-74.25, -64.25) * mm, "mid": v(-71.32, -71.32) * mm, "end": v(-64.25, -74.25) * mm});
            skArc(sketch, "E94.4", {"start": v(74.25, 64.25) * mm, "mid": v(71.32, 71.32) * mm, "end": v(64.25, 74.25) * mm});
            skLineSegment(sketch, "E94.5", {"start": v(74.25, -64.25) * mm, "end": v(74.25, 64.25) * mm});
            skArc(sketch, "E94.6", {"start": v(64.25, -74.25) * mm, "mid": v(71.32, -71.32) * mm, "end": v(74.25, -64.25) * mm});
            skLineSegment(sketch, "E94.7", {"start": v(-64.25, -74.25) * mm, "end": v(64.25, -74.25) * mm});
            skCircle(sketch, "E95.0", {"center": v(60, 67.5) * mm, "radius": 4 * mm});
            skCircle(sketch, "E96.0", {"center": v(-60, 67.5) * mm, "radius": 4 * mm});
            skCircle(sketch, "E97.0", {"center": v(-60, -67.5) * mm, "radius": 4 * mm});
            skCircle(sketch, "E98.0", {"center": v(60, -67.5) * mm, "radius": 4 * mm});
            skArc(sketch, "E99.0", {"start": v(56.15, 48.18) * mm, "mid": v(0, 67.5) * mm, "end": v(-56.15, 48.18) * mm});
            skArc(sketch, "E99.1", {"start": v(60, 40.3) * mm, "mid": v(58.99, 44.68) * mm, "end": v(56.15, 48.18) * mm});
            skArc(sketch, "E99.2", {"start": v(-56.15, 48.18) * mm, "mid": v(-58.99, 44.68) * mm, "end": v(-60, 40.3) * mm});
            skLineSegment(sketch, "E99.3", {"start": v(60, 40.3) * mm, "end": v(60, -40.3) * mm});
            skLineSegment(sketch, "E99.4", {"start": v(-60, 40.3) * mm, "end": v(-60, -40.3) * mm});
            skArc(sketch, "E99.5", {"start": v(-60, -40.3) * mm, "mid": v(-58.99, -44.68) * mm, "end": v(-56.15, -48.18) * mm});
            skArc(sketch, "E99.6", {"start": v(-56.15, -48.18) * mm, "mid": v(0, -67.5) * mm, "end": v(56.15, -48.18) * mm});
            skArc(sketch, "E99.7", {"start": v(56.15, -48.18) * mm, "mid": v(58.99, -44.68) * mm, "end": v(60, -40.3) * mm});
            skSolve(sketch);
        }
        {
            var Q0;
            Q0 = qSketchRegion(id + "F16", true);
            var Q1;
            Q1=makeQuery(id+"F2.opExtrude","CAP_FACE",FACE,{"disambiguationData":[OSD([sQuery(id+"F0.wireOp",EDGE,"E12"),sQuery(id+"F0.wireOp",EDGE,"E13"),sQuery(id+"F0.wireOp",EDGE,"E14"),sQuery(id+"F0.wireOp",EDGE,"E15"),sQuery(id+"F0.wireOp",EDGE,"E17.filletArc"),sQuery(id+"F0.wireOp",EDGE,"E18.filletArc"),sQuery(id+"F0.wireOp",EDGE,"E19.filletArc"),sQuery(id+"F0.wireOp",EDGE,"E20.filletArc"),sQuery(id+"F0.wireOp",EDGE,"E25.0"),sQuery(id+"F0.wireOp",EDGE,"E25.1"),sQuery(id+"F0.wireOp",EDGE,"E25.2"),sQuery(id+"F0.wireOp",EDGE,"E25.3"),sQuery(id+"F0.wireOp",EDGE,"E25.4"),sQuery(id+"F0.wireOp",EDGE,"E25.5"),sQuery(id+"F0.wireOp",EDGE,"E25.6"),sQuery(id+"F0.wireOp",EDGE,"E25.7")])],"isStart":false});
            extrude(context, id + "F17", {"entities" : qUnion([Q0]), "endBound" : BoundingType.UP_TO_SURFACE, "endBoundEntityFace" : qUnion([Q1]), "depth" : 25 * mm});
        }
    });
